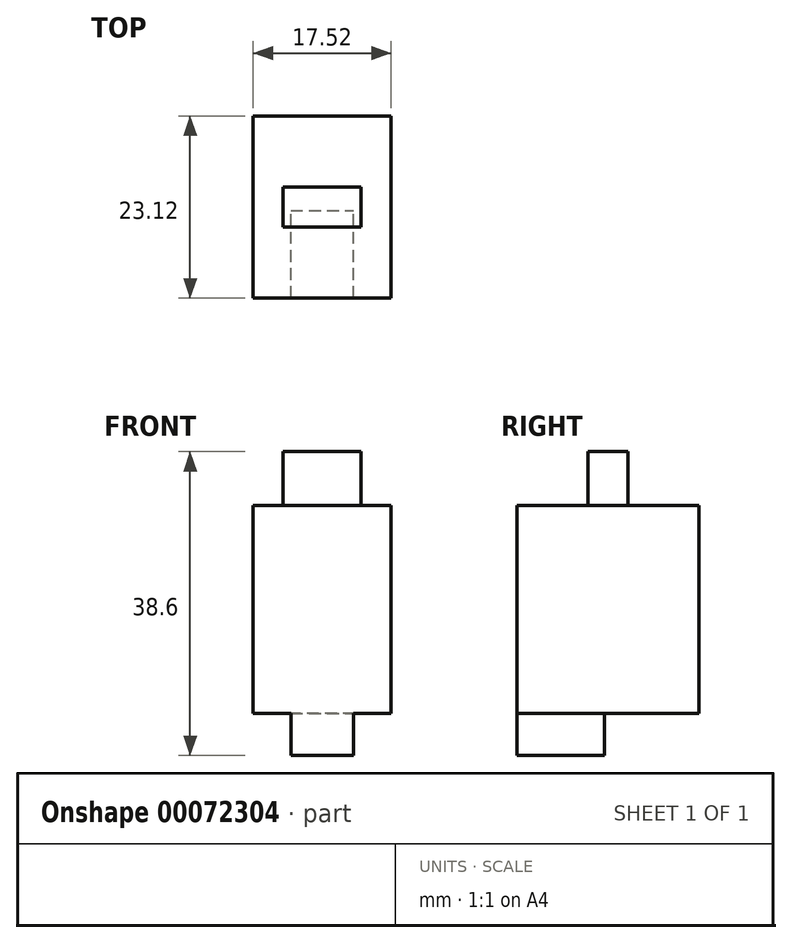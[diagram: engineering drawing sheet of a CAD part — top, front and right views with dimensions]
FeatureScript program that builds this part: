
annotation { "Feature Type Name" : "Feature", "Feature Type Description" : "" }
export const myFeature = defineFeature(function(context is Context, id is Id, definition is map)
    precondition{}
    {
        {
            var Q0;
            Q0=qCreatedBy(makeId("Top.planeOp"),FACE);
            var sketch = newSketch(context, id + "F0", { "sketchPlane" : qUnion([Q0])});
            skLineSegment(sketch, "E0.bottom", {"start": v(8.76, -11.56) * mm, "end": v(-8.76, -11.56) * mm});
            skLineSegment(sketch, "E0.top", {"start": v(8.76, 11.56) * mm, "end": v(-8.76, 11.56) * mm});
            skLineSegment(sketch, "E0.left", {"start": v(8.76, -11.56) * mm, "end": v(8.76, 11.56) * mm});
            skLineSegment(sketch, "E0.right", {"start": v(-8.76, -11.56) * mm, "end": v(-8.76, 11.56) * mm});
            skPoint(sketch, "E0.middle", {"position": v(0, 0) * mm});
            skSolve(sketch);
        }
        {
            var Q0;
            Q0 = qSketchRegion(id + "F0", true);
            extrude(context, id + "F1", {"entities" : qUnion([Q0]), "depth" : 26.42 * mm});
        }
        {
            var Q0;
            Q0=makeQuery(id+"F1.opExtrude","CAP_FACE",FACE,{"disambiguationData":[OSD([sQuery(id+"F0.wireOp",EDGE,"E0.bottom"),sQuery(id+"F0.wireOp",EDGE,"E0.top"),sQuery(id+"F0.wireOp",EDGE,"E0.left"),sQuery(id+"F0.wireOp",EDGE,"E0.right")])],"isStart":false});
            var sketch = newSketch(context, id + "F2", { "sketchPlane" : qUnion([Q0])});
            skLineSegment(sketch, "E1.bottom", {"start": v(4.95, -2.53) * mm, "end": v(-4.95, -2.53) * mm});
            skLineSegment(sketch, "E1.top", {"start": v(4.95, 2.53) * mm, "end": v(-4.95, 2.53) * mm});
            skLineSegment(sketch, "E1.left", {"start": v(4.95, -2.53) * mm, "end": v(4.95, 2.53) * mm});
            skLineSegment(sketch, "E1.right", {"start": v(-4.95, -2.53) * mm, "end": v(-4.95, 2.53) * mm});
            skPoint(sketch, "E1.middle", {"position": v(0, 0) * mm});
            skSolve(sketch);
        }
        {
            var Q0;
            Q0 = qSketchRegion(id + "F2", true);
            extrude(context, id + "F3", {"entities" : qUnion([Q0]), "operationType" : NewBodyOperationType.ADD, "depth" : 6.86 * mm});
        }
        {
            var Q0;
            Q0=makeQuery(id+"F1.opExtrude","CAP_FACE",FACE,{"disambiguationData":[OSD([sQuery(id+"F0.wireOp",EDGE,"E0.bottom"),sQuery(id+"F0.wireOp",EDGE,"E0.top"),sQuery(id+"F0.wireOp",EDGE,"E0.left"),sQuery(id+"F0.wireOp",EDGE,"E0.right")])],"isStart":true});
            var sketch = newSketch(context, id + "F4", { "sketchPlane" : qUnion([Q0])});
            skLineSegment(sketch, "E2.bottom", {"start": v(-3.97, 11.56) * mm, "end": v(3.97, 11.56) * mm});
            skLineSegment(sketch, "E2.top", {"start": v(-3.97, 0.44) * mm, "end": v(3.97, 0.44) * mm});
            skLineSegment(sketch, "E2.left", {"start": v(-3.97, 11.56) * mm, "end": v(-3.97, 0.44) * mm});
            skLineSegment(sketch, "E2.right", {"start": v(3.97, 11.56) * mm, "end": v(3.97, 0.44) * mm});
            skPoint(sketch, "E2.middle", {"position": v(0, 6) * mm});
            skSolve(sketch);
        }
        {
            var Q0;
            Q0 = qSketchRegion(id + "F4", true);
            extrude(context, id + "F5", {"entities" : qUnion([Q0]), "operationType" : NewBodyOperationType.ADD, "depth" : 5.33 * mm});
        }
    });
